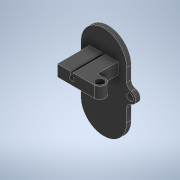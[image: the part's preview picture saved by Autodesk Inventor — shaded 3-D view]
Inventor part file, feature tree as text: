
AUTODESK INVENTOR PART (.ipt)
format: ipt  version: 2021 (Build 250183000, 183)  size: 192,000 bytes
history: native  units: mm
features: extrude x5, sketch x5, projected_geometry x4, fillet x1
ambient origin geometry x8: Origin, YZ Plane, XZ Plane, XY Plane, X Axis, Y Axis, Z Axis, Center Point
bodies: Solid1 (feature_tree)
feature tree (15):
  extrude  "Extrusion1"  Depth=10.0mm
  extrude  "Extrusion2"  Depth=2.0mm TaperAngle=0.0deg
  fillet  "Fillet1"  Radius=23.0mm
  sketch  "Sketch3"  dims[d8=3.0mm d9=3.0mm]
  extrude  "Extrusion3"  Depth=3.0mm
  extrude  "Extrusion4"  Depth=5.0mm
  extrude  "Extrusion5"  Depth=2.5mm
  sketch  "Sketch1"  dims[d0=20.9mm d3=10.0mm]
  sketch  "Sketch2"  dims[d4=10.0mm d5=2.0mm d6=0.0mm d7=23.0mm]
  projected_geometry  "Projected Loop1"
  projected_geometry  "Projected Loop2"
  sketch  "Sketch4"  dims[d10=5.0mm d11=5.0mm]
  projected_geometry  "Projected Loop3"
  sketch  "Sketch5"  dims[d12=2.0mm d13=0.0mm d14=2.5mm d20=5.8mm d21=5.0mm d22=5.0mm d23=14.0mm d24=0.0mm d25=1.0mm d27=2.0mm d28=14.0mm d29=0.0mm d30=3.5mm d33=3.5mm d34=5.0mm d35=0.0mm]
  projected_geometry  "Projected Loop4"
